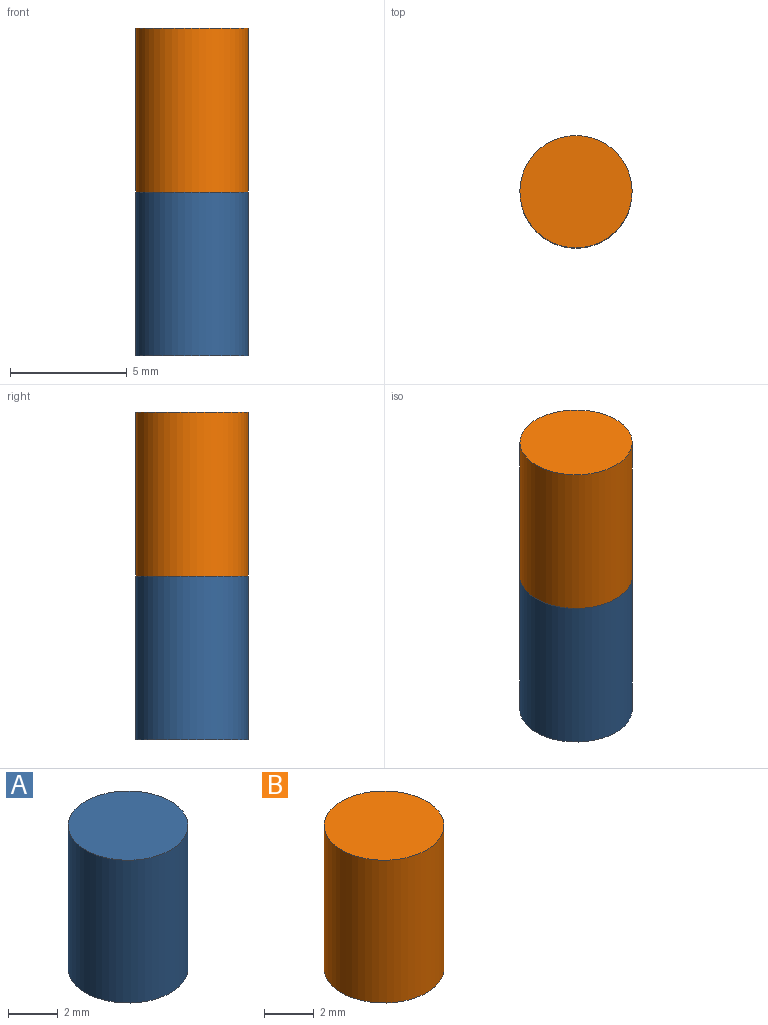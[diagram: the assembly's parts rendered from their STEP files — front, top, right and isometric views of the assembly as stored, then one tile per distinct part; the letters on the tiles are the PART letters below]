
ASSEMBLY  parts=2 mates=1
PART A: 3 faces, bbox 4.8x4.8x7 mm
  f0: cylinder r=2.4mm len=7mm, axis (0,0,1), area 105.6mm2, adj f1,f2
  f1: plane 4.8x4.8mm, normal (0,0,1), area 18.1mm2, adj f0
  f2: plane 4.8x4.8mm, normal (0,0,-1), area 18.1mm2, adj f0
PART B: 3 faces, bbox 4.8x4.8x7 mm
  f0: cylinder r=2.4mm len=7mm, axis (0,0,-1), area 105.6mm2, adj f1,f2
  f1: plane 4.8x4.8mm, normal (0,0,1), area 18.1mm2, adj f0
  f2: plane 4.8x4.8mm, normal (0,0,-1), area 18.1mm2, adj f0
PLACE A at identity
PLACE B at identity
MATE fastened B.f0 <-> A.f0  axis (0,0,-1) through (0,0,0)mm
